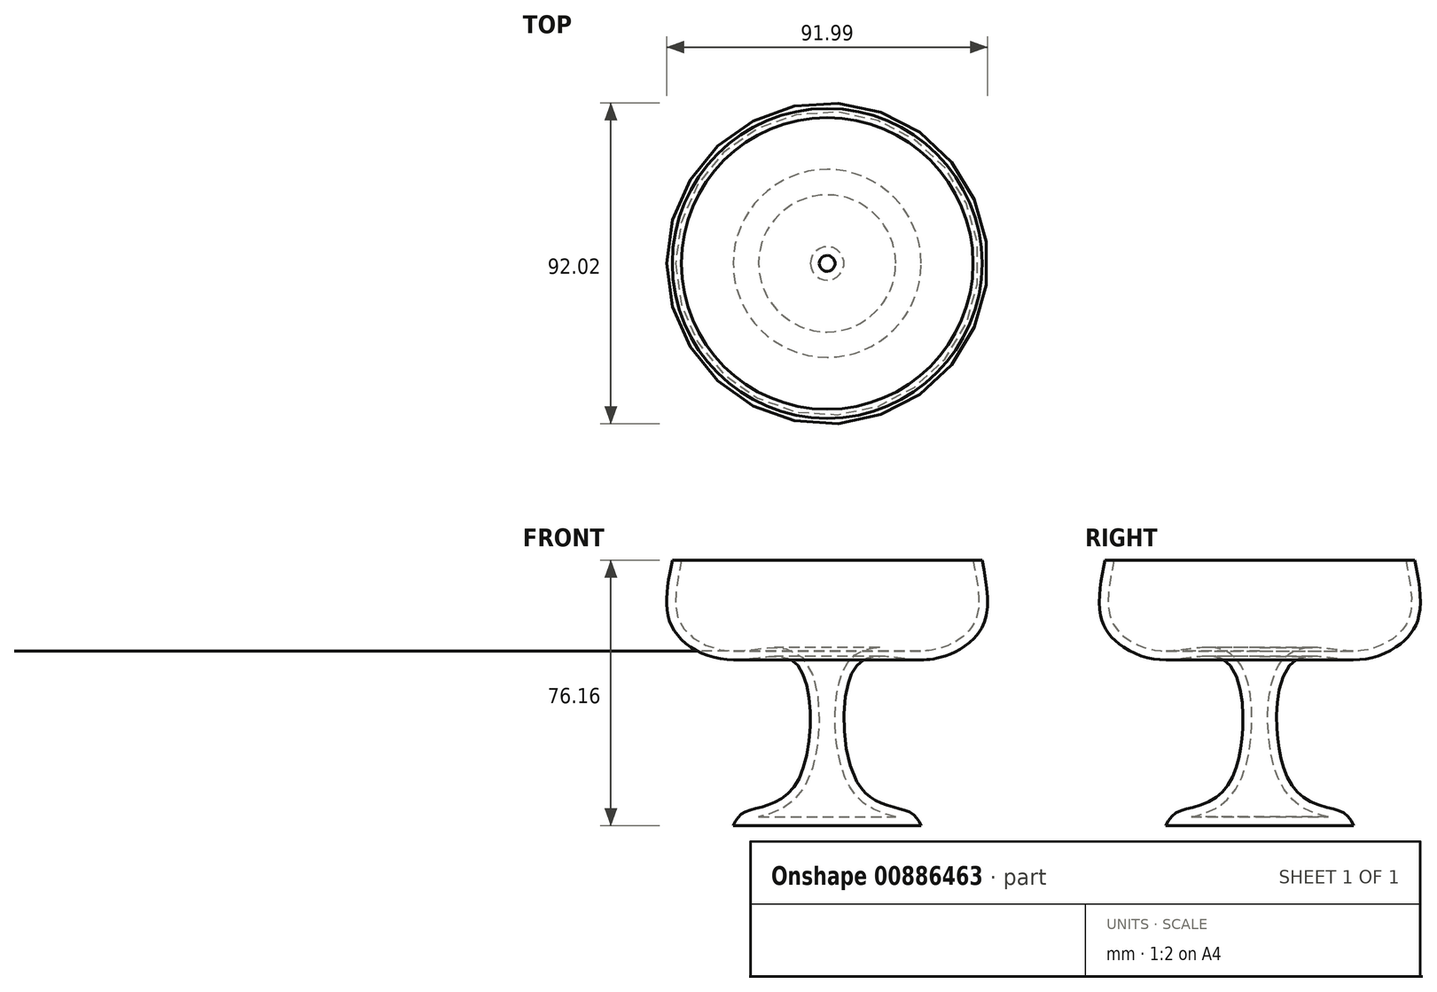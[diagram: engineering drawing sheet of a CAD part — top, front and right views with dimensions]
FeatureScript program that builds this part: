
annotation { "Feature Type Name" : "Feature", "Feature Type Description" : "" }
export const myFeature = defineFeature(function(context is Context, id is Id, definition is map)
    precondition{}
    {
        {
            var Q0;
            Q0=qCreatedBy(makeId("Front.planeOp"),FACE);
            var sketch = newSketch(context, id + "F0", { "sketchPlane" : qUnion([Q0])});
            skLineSegment(sketch, "E0", {"start": v(0, 0) * mm, "end": v(44.39, 0) * mm});
            skFitSpline(sketch, "E1", {"points": [v(44.39, 0) * mm, v(44.39, -19.28) * mm, v(27.59, -28.62) * mm, v(8.94, -29.68) * mm, v(7.7, -61.82) * mm, v(17.85, -70.52) * mm, v(24.25, -72.6) * mm, v(26.92, -76.16) * mm], "startDerivative": vector(26.72, -135.74) * mm, "endDerivative": vector(23.88, -55.9) * mm});
            skLineSegment(sketch, "E2", {"start": v(26.92, -76.16) * mm, "end": v(0, -76.16) * mm});
            skLineSegment(sketch, "E3", {"start": v(0, -76.16) * mm, "end": v(0, 0) * mm});
            skSolve(sketch);
        }
        {
            var Q0;
            Q0 = qSketchRegion(id + "F0", true);
            var Q1;
            Q1=sQuery(id+"F0.wireOp",EDGE,"E3");
            revolve(context, id + "F1", {"surfaceOperationType" : NewSurfaceOperationType.NEW, "entities" : qUnion([Q0]), "axis" : qUnion([Q1]), "revolveType" : RevolveType.FULL});
        }
        {
            var Q0;
            Q0=makeQuery(id+"F1.opRevolve","SWEPT_FACE",FACE,{"disambiguationData":[OSD([sQuery(id+"F0.wireOp",EDGE,"E0")])]});
            shell(context, id + "F2", {"entities" : qUnion([Q0]), "thickness" : 2.54 * mm});
        }
    });
